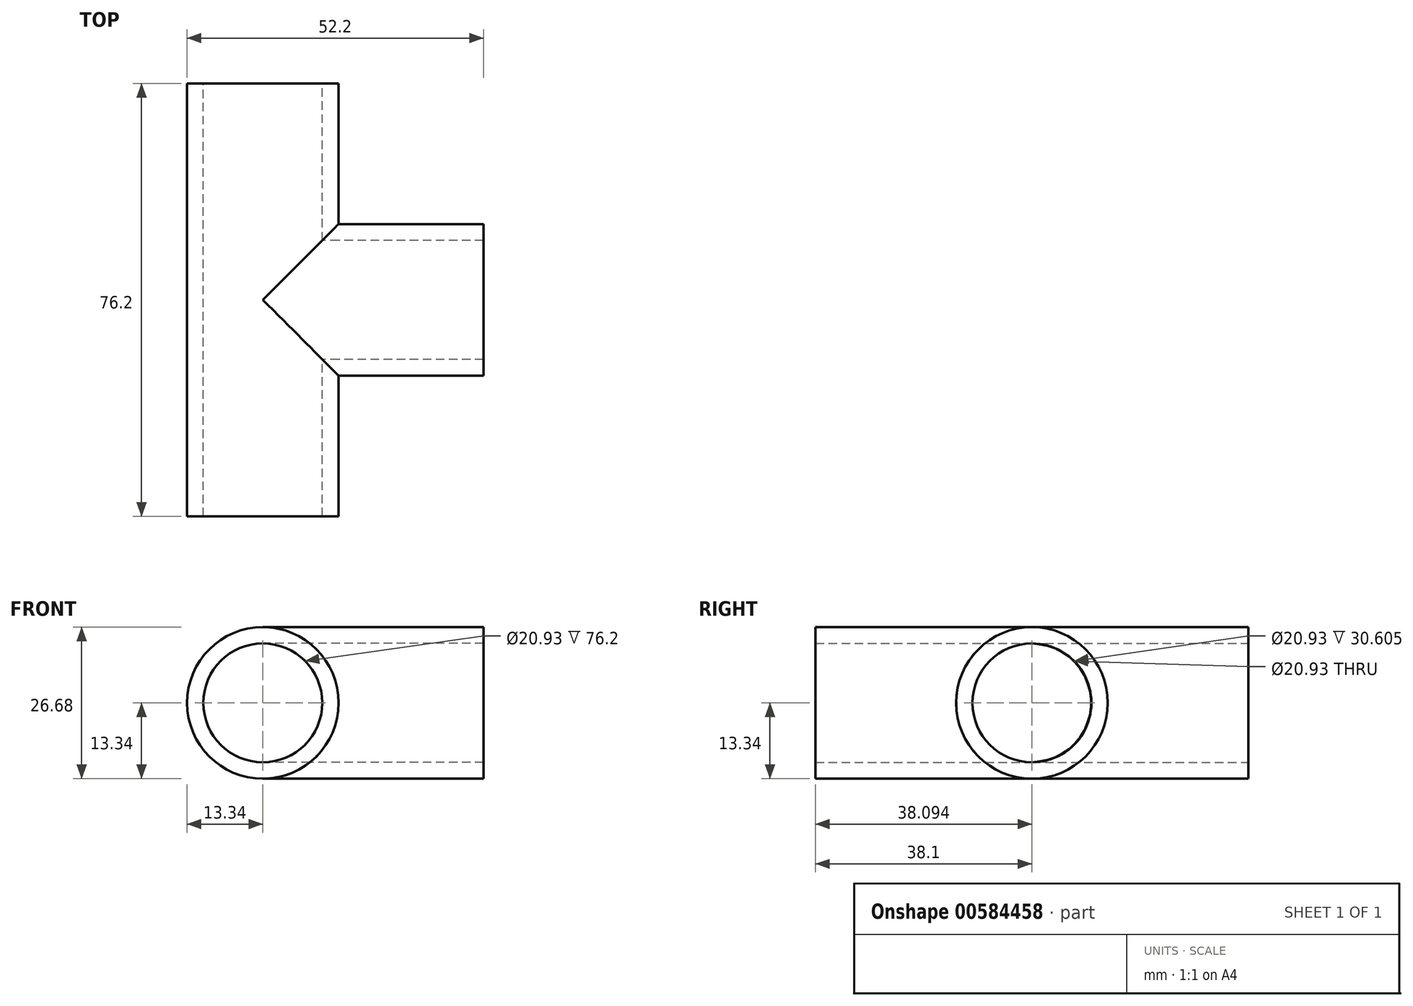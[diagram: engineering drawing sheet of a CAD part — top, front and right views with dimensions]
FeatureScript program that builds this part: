
annotation { "Feature Type Name" : "Feature", "Feature Type Description" : "" }
export const myFeature = defineFeature(function(context is Context, id is Id, definition is map)
    precondition{}
    {
        {
            var Q0;
            Q0=qCreatedBy(makeId("Front.planeOp"),FACE);
            var sketch = newSketch(context, id + "F0", { "sketchPlane" : qUnion([Q0])});
            skCircle(sketch, "E0", {"center": v(0, 0) * mm, "radius": 13.33 * mm});
            skCircle(sketch, "E1", {"center": v(0, 0) * mm, "radius": 10.46 * mm});
            skSolve(sketch);
        }
        {
            var Q0;
            Q0=qCreatedBy(makeId("Right.planeOp"),FACE);
            var sketch = newSketch(context, id + "F1", { "sketchPlane" : qUnion([Q0])});
            skLineSegment(sketch, "E2", {"start": v(0, 0) * mm, "end": v(76.2, 0) * mm});
            skSolve(sketch);
        }
        {
            var Q0;
            Q0=makeQuery(id+"F0.imprint","IMPRINT",FACE,{"disambiguationData":[TD([[makeQuery(id+"F0.imprint","IMPRINT",EDGE,{"derivedFrom":sQuery(id+"F0.wireOp",EDGE,"E0")}),1.0]])]});
            var Q1;
            Q1=sQuery(id+"F1.wireOp",EDGE,"E2");
            sweep(context, id + "F2", {"profiles" : qUnion([Q0]), "path" : qUnion([Q1])});
        }
        {
            var Q0;
            Q0=qCreatedBy(makeId("Right.planeOp"),FACE);
            var sketch = newSketch(context, id + "F3", { "sketchPlane" : qUnion([Q0])});
            skLineSegment(sketch, "E3.left", {"start": v(76.19, -14.7) * mm, "end": v(76.19, 11.97) * mm, "construction": true});
            skPoint(sketch, "E3.middle", {"position": v(0, 0) * mm});
            skLineSegment(sketch, "E4", {"start": v(0, -13.33) * mm, "end": v(0, 13.34) * mm, "construction": true});
            skPoint(sketch, "E3.right.end.orphan", {"position": v(-76.19, 14.7) * mm});
            skPoint(sketch, "E3.right.start.orphan", {"position": v(-76.19, -11.97) * mm});
            skLineSegment(sketch, "E5", {"start": v(0, -13.33) * mm, "end": v(76.19, -13.33) * mm, "construction": true});
            skLineSegment(sketch, "E6", {"start": v(0, 13.34) * mm, "end": v(76.2, 13.34) * mm, "construction": true});
            skLineSegment(sketch, "E7", {"start": v(76.2, 13.34) * mm, "end": v(76.19, -13.33) * mm, "construction": true});
            skLineSegment(sketch, "E8", {"start": v(0, 0) * mm, "end": v(76.19, 0) * mm, "construction": true});
            skCircle(sketch, "E9", {"center": v(38.1, 0) * mm, "radius": 10.46 * mm});
            skSolve(sketch);
        }
        {
            var Q0;
            Q0=qSketchRegion(id+"F3",true);
            extrude(context, id + "F4", {"entities" : qUnion([Q0]), "operationType" : NewBodyOperationType.REMOVE, "depth" : 24.13 * mm, "offsetDistance" : 25.4 * mm});
        }
        {
            var Q0;
            Q0=qCreatedBy(makeId("Right.planeOp"),FACE);
            var sketch = newSketch(context, id + "F5", { "sketchPlane" : qUnion([Q0])});
            skLineSegment(sketch, "E10.bottom", {"start": v(76.2, -13.33) * mm, "end": v(0, -13.34) * mm, "construction": true});
            skLineSegment(sketch, "E10.top", {"start": v(76.2, 13.34) * mm, "end": v(0, 13.34) * mm, "construction": true});
            skLineSegment(sketch, "E10.left", {"start": v(76.2, -13.33) * mm, "end": v(76.2, 13.34) * mm, "construction": true});
            skPoint(sketch, "E10.middle", {"position": v(0, 0) * mm});
            skLineSegment(sketch, "E11", {"start": v(0, -13.34) * mm, "end": v(0, 13.34) * mm, "construction": true});
            skLineSegment(sketch, "E12", {"start": v(0, 13.34) * mm, "end": v(0, 0) * mm, "construction": true});
            skLineSegment(sketch, "E13", {"start": v(76.2, 0) * mm, "end": v(0, 0) * mm, "construction": true});
            skPoint(sketch, "E10.right.end.orphan", {"position": v(-76.2, 13.33) * mm});
            skPoint(sketch, "E10.right.start.orphan", {"position": v(-76.2, -13.34) * mm});
            skCircle(sketch, "E14", {"center": v(38.1, 0) * mm, "radius": 13.34 * mm});
            skCircle(sketch, "E15", {"center": v(38.1, 0) * mm, "radius": 10.46 * mm});
            skSolve(sketch);
        }
        {
            var Q0;
            Q0=qSketchRegion(id+"F5",true);
            extrude(context, id + "F6", {"entities" : qUnion([Q0]), "operationType" : NewBodyOperationType.ADD, "depth" : 38.86 * mm, "offsetDistance" : 25.4 * mm});
        }
        {
            var Q0;
            Q0=qCreatedBy(makeId("Front.planeOp"),FACE);
            var sketch = newSketch(context, id + "F7", { "sketchPlane" : qUnion([Q0])});
            skCircle(sketch, "E16", {"center": v(0, 0) * mm, "radius": 10.46 * mm});
            skSolve(sketch);
        }
        {
            var Q0;
            Q0=qSketchRegion(id+"F7",true);
            extrude(context, id + "F8", {"entities" : qUnion([Q0]), "operationType" : NewBodyOperationType.REMOVE, "oppositeDirection" : true, "depth" : 91.7 * mm, "offsetDistance" : 25.4 * mm});
        }
    });
